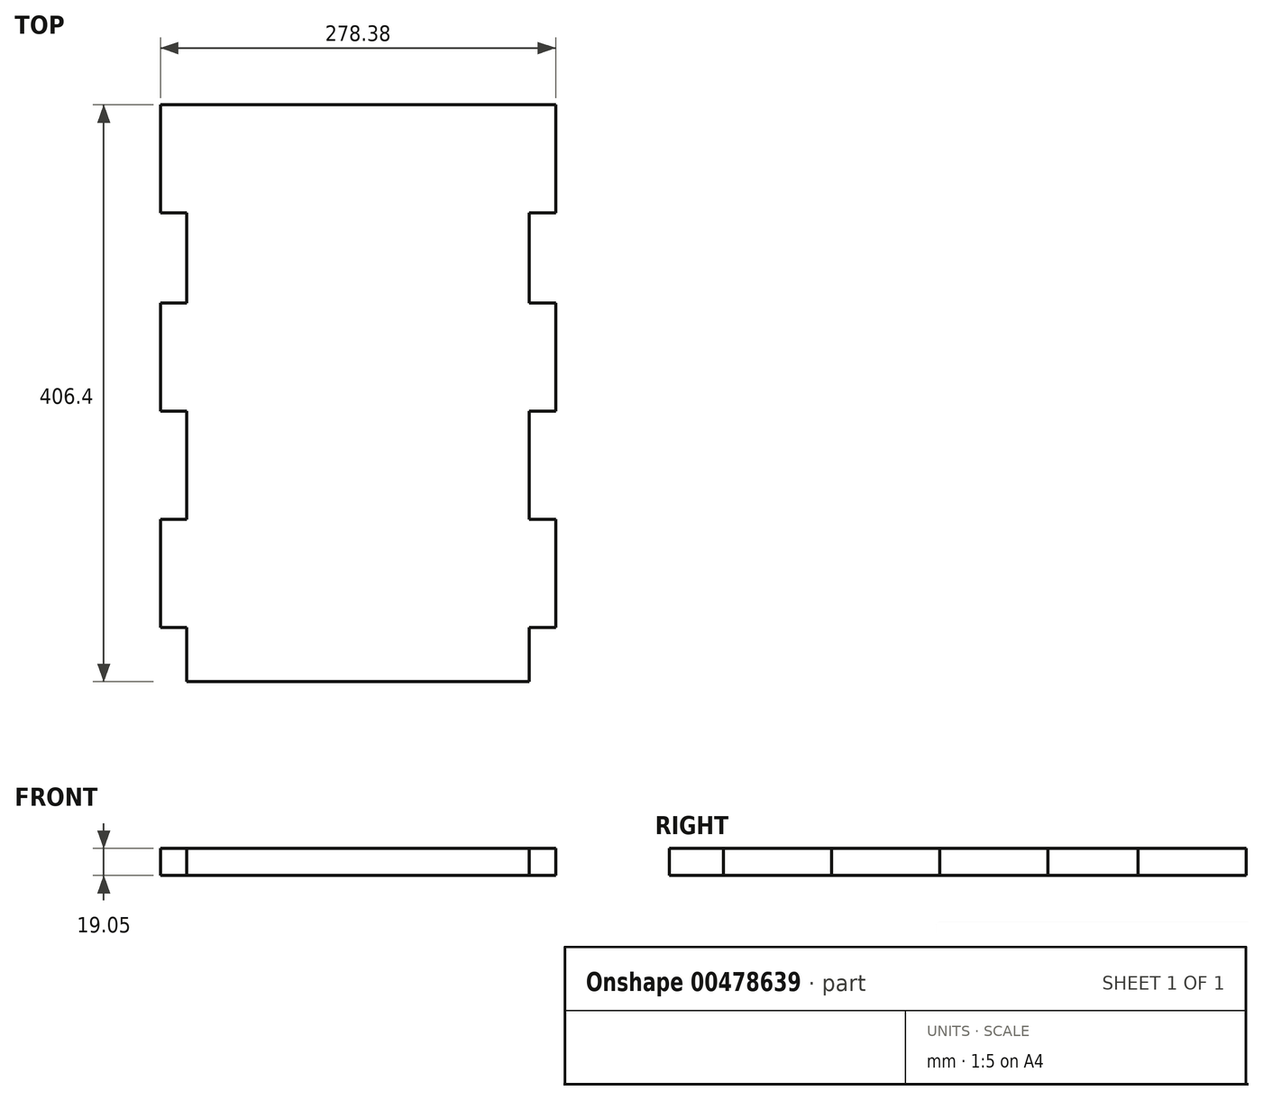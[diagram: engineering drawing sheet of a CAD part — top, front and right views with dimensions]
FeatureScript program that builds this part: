
annotation { "Feature Type Name" : "Feature", "Feature Type Description" : "" }
export const myFeature = defineFeature(function(context is Context, id is Id, definition is map)
    precondition{}
    {
        {
            var Q0;
            Q0=qCreatedBy(makeId("Top.planeOp"),FACE);
            var sketch = newSketch(context, id + "F0", { "sketchPlane" : qUnion([Q0])});
            skLineSegment(sketch, "E0.bottom", {"start": v(-223.37, 245.65) * mm, "end": v(17.93, 245.65) * mm});
            skLineSegment(sketch, "E0.top", {"start": v(-223.37, -160.75) * mm, "end": v(17.93, -160.75) * mm});
            skLineSegment(sketch, "E0.left", {"start": v(-223.37, 245.65) * mm, "end": v(-223.37, -160.75) * mm});
            skLineSegment(sketch, "E0.right", {"start": v(17.93, 245.65) * mm, "end": v(17.93, -160.75) * mm});
            skLineSegment(sketch, "E1.bottom", {"start": v(17.93, 245.65) * mm, "end": v(36.47, 245.65) * mm});
            skLineSegment(sketch, "E1.top", {"start": v(17.93, 169.45) * mm, "end": v(36.47, 169.45) * mm});
            skLineSegment(sketch, "E1.left", {"start": v(17.93, 245.65) * mm, "end": v(17.93, 169.45) * mm});
            skLineSegment(sketch, "E1.right", {"start": v(36.47, 245.65) * mm, "end": v(36.47, 169.45) * mm});
            skPoint(sketch, "E2.oppositeSnap0", {"position": v(36.47, 207.55) * mm});
            skLineSegment(sketch, "E2.bottom", {"start": v(17.93, 105.95) * mm, "end": v(36.47, 105.95) * mm});
            skLineSegment(sketch, "E2.top", {"start": v(17.93, 29.75) * mm, "end": v(36.47, 29.75) * mm});
            skLineSegment(sketch, "E2.left", {"start": v(17.93, 105.95) * mm, "end": v(17.93, 29.75) * mm});
            skLineSegment(sketch, "E2.right", {"start": v(36.47, 105.95) * mm, "end": v(36.47, 29.75) * mm});
            skLineSegment(sketch, "E3.bottom", {"start": v(17.93, -46.45) * mm, "end": v(36.47, -46.45) * mm});
            skLineSegment(sketch, "E3.top", {"start": v(17.93, -122.65) * mm, "end": v(36.47, -122.65) * mm});
            skLineSegment(sketch, "E3.left", {"start": v(17.93, -46.45) * mm, "end": v(17.93, -122.65) * mm});
            skLineSegment(sketch, "E3.right", {"start": v(36.47, -46.45) * mm, "end": v(36.47, -122.65) * mm});
            skLineSegment(sketch, "E4", {"start": v(-102.72, 245.65) * mm, "end": v(-102.72, -160.75) * mm, "construction": true});
            skLineSegment(sketch, "E5.MirrorCS", {"start": v(-223.37, 169.45) * mm, "end": v(-241.91, 169.45) * mm});
            skLineSegment(sketch, "E6.MirrorCS", {"start": v(-241.91, 245.65) * mm, "end": v(-241.91, 169.45) * mm});
            skLineSegment(sketch, "E7.MirrorCS", {"start": v(-223.37, 245.65) * mm, "end": v(-241.91, 245.65) * mm});
            skLineSegment(sketch, "E8.MirrorCS", {"start": v(-223.37, 105.95) * mm, "end": v(-241.91, 105.95) * mm});
            skLineSegment(sketch, "E9.MirrorCS", {"start": v(-241.91, 105.95) * mm, "end": v(-241.91, 29.75) * mm});
            skLineSegment(sketch, "E10.MirrorCS", {"start": v(-223.37, 29.75) * mm, "end": v(-241.91, 29.75) * mm});
            skLineSegment(sketch, "E11.MirrorCS", {"start": v(-223.37, -46.45) * mm, "end": v(-241.91, -46.45) * mm});
            skLineSegment(sketch, "E12.MirrorCS", {"start": v(-241.91, -46.45) * mm, "end": v(-241.91, -122.65) * mm});
            skLineSegment(sketch, "E13.MirrorCS", {"start": v(-223.37, -122.65) * mm, "end": v(-241.91, -122.65) * mm});
            skSolve(sketch);
        }
        {
            var Q0;
            {var subQ10=sQuery(id+"F0.wireOp",EDGE,"E0.bottom");Q0=makeQuery(id+"F0.imprint","IMPRINT",FACE,{"disambiguationData":[TD([[makeQuery(id+"F0.imprint","IMPRINT",EDGE,{"derivedFrom":subQ10}),-1.0]])]});}
            var Q1;
            Q1=makeQuery(id+"F0.imprint","IMPRINT",FACE,{"disambiguationData":[TD([[makeQuery(id+"F0.imprint","IMPRINT",EDGE,{"derivedFrom":sQuery(id+"F0.wireOp",EDGE,"E1.bottom")}),-1.0]])]});
            var Q2;
            Q2=makeQuery(id+"F0.imprint","IMPRINT",FACE,{"disambiguationData":[TD([[makeQuery(id+"F0.imprint","IMPRINT",EDGE,{"derivedFrom":sQuery(id+"F0.wireOp",EDGE,"E2.bottom")}),-1.0]])]});
            var Q3;
            Q3=makeQuery(id+"F0.imprint","IMPRINT",FACE,{"disambiguationData":[TD([[makeQuery(id+"F0.imprint","IMPRINT",EDGE,{"derivedFrom":sQuery(id+"F0.wireOp",EDGE,"E3.bottom")}),-1.0]])]});
            var Q4;
            {var subQ0=sQuery(id+"F0.wireOp",EDGE,"E11.MirrorCS");Q4=makeQuery(id+"F0.imprint","IMPRINT",FACE,{"disambiguationData":[TD([[makeQuery(id+"F0.imprint","IMPRINT",EDGE,{"derivedFrom":subQ0}),1.0]])]});}
            var Q5;
            {var subQ0=sQuery(id+"F0.wireOp",EDGE,"E8.MirrorCS");Q5=makeQuery(id+"F0.imprint","IMPRINT",FACE,{"disambiguationData":[TD([[makeQuery(id+"F0.imprint","IMPRINT",EDGE,{"derivedFrom":subQ0}),1.0]])]});}
            var Q6;
            {var subQ2=sQuery(id+"F0.wireOp",EDGE,"E5.MirrorCS");Q6=makeQuery(id+"F0.imprint","IMPRINT",FACE,{"disambiguationData":[TD([[makeQuery(id+"F0.imprint","IMPRINT",EDGE,{"derivedFrom":subQ2}),-1.0]])]});}
            extrude(context, id + "F1", {"entities" : qUnion([Q0, Q1, Q2, Q3, Q4, Q5, Q6]), "depth" : 19.05 * mm, "offsetDistance" : 25.4 * mm});
        }
    });
